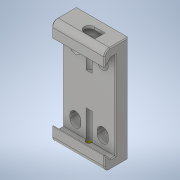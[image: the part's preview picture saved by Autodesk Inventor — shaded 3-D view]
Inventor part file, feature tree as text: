
AUTODESK INVENTOR PART (.ipt)
format: ipt  version: 2021.1 (Build 251245010, 245A)  size: 227,840 bytes
history: mixed  units: in
note: dims shown in document units (in); Inventor stores cm internally (conversion verified against a paired STEP export)
features: extrude x3, sketch x2, direct_edit x1, move_body x1, imported_body x1
ambient origin geometry x8: Origin, YZ Plane, XZ Plane, XY Plane, X Axis, Y Axis, Z Axis, Center Point
bodies: Solid1 (imported_parasolid), Body6 (imported_parasolid)
feature tree (8):
  extrude  "Extrusion1"  Depth=0.6299in TaperAngle=0.0deg
  sketch  "Skizze2"  dims[d4=0.0984in d5=0.0in d6=0.0in d7=0.0in d8=0.1969in]
  extrude  "Extrusion2"  Depth=0.1969in TaperAngle=0.0deg
  extrude  "Extrusion3"  [1 undecoded]
  direct_edit  "Direktbearbeitung1"
  sketch  "Skizze1"  dims[d0=0.1575in d1=0.0in d2=0.6299in d3=0.0in]
  move_body  "Verschieben1"
  imported_body  NMx_Import_Brep_tag  [imported B-rep: ~27 faces, bbox_mm=[28.0, 20.0, 10.0]]
note: 1 required parameter value undecoded (feature->parameter linkage not recoverable at this tier; creation-order binding heuristic only, values carry confidence <= 0.55)
